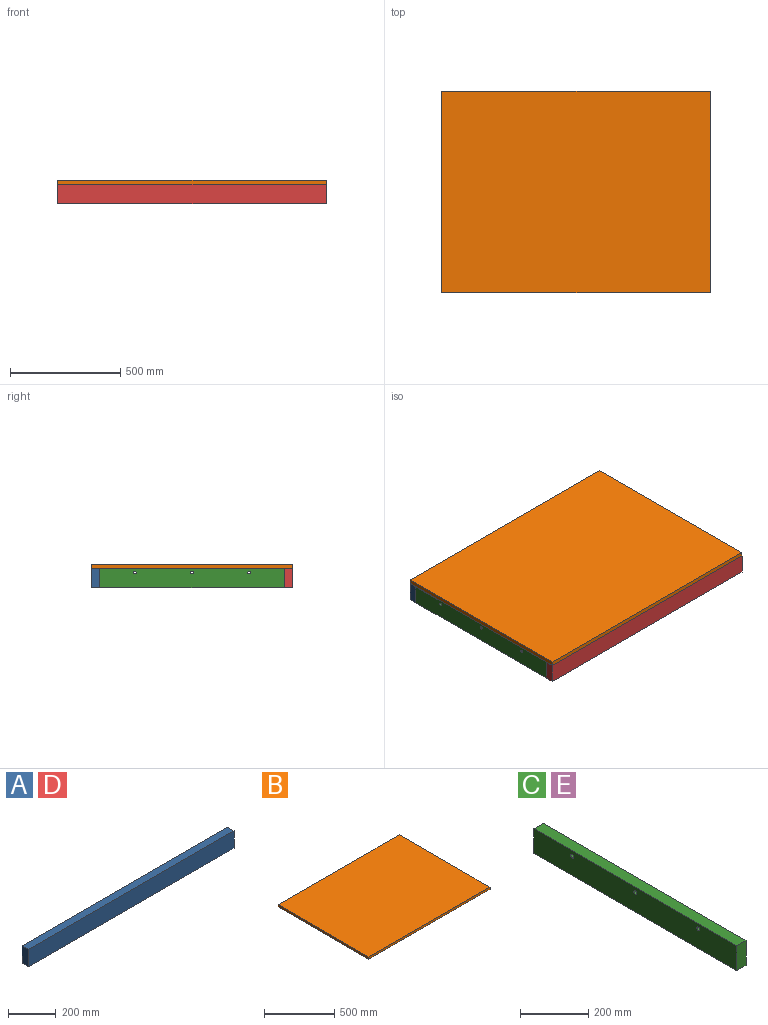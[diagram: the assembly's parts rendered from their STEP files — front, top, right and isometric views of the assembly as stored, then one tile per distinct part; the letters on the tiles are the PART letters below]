
ASSEMBLY  parts=5 mates=12
PART A: 6 faces, bbox 1219.2x38.1x88.9 mm
  f0: plane 1219.2x38.1mm, normal (0,0,1), area 46451.5mm2, adj f1,f3,f4,f5
  f1: plane 1219.2x88.9mm, normal (0,-1,0), area 108386.9mm2, adj f0,f2,f4,f5
  f2: plane 1219.2x38.1mm, normal (0,0,-1), area 46451.5mm2, adj f1,f3,f4,f5
  f3: plane 1219.2x88.9mm, normal (0,1,0), area 108386.9mm2, adj f0,f2,f4,f5
  f4: plane 88.9x38.1mm, normal (-1,0,0), area 3387.1mm2, adj f0,f1,f2,f3
  f5: plane 88.9x38.1mm, normal (1,0,0), area 3387.1mm2, adj f0,f1,f2,f3
PART B: 6 faces, bbox 1219.2x914.4x19.1 mm
  f0: plane 1219.2x19.05mm, normal (0,1,0), area 23225.8mm2, adj f1,f3,f4,f5
  f1: plane 914.4x19.05mm, normal (-1,0,0), area 17419.3mm2, adj f0,f2,f4,f5
  f2: plane 1219.2x19.05mm, normal (0,-1,0), area 23225.8mm2, adj f1,f3,f4,f5
  f3: plane 914.4x19.05mm, normal (1,0,0), area 17419.3mm2, adj f0,f2,f4,f5
  f4: plane 1219.2x914.4mm, normal (0,0,1), area 1114836.5mm2, adj f0,f1,f2,f3
  f5: plane 1219.2x914.4mm, normal (0,0,-1), area 1114836.5mm2, adj f0,f1,f2,f3
PART C: 9 faces, bbox 38.1x838.2x88.9 mm
  f0: plane 838.2x38.1mm, normal (0,0,1), area 31935.4mm2, adj f1,f3,f4,f5
  f1: plane 838.2x88.9mm, normal (-1,0,0), area 74135.9mm2, adj f0,f2,f4,f5,f6,f7,f8
  f2: plane 838.2x38.1mm, normal (0,0,-1), area 31935.4mm2, adj f1,f3,f4,f5
  f3: plane 838.2x88.9mm, normal (1,0,0), area 74135.9mm2, adj f0,f2,f4,f5,f6,f7,f8
  f4: plane 88.9x38.1mm, normal (0,1,0), area 3387.1mm2, adj f0,f1,f2,f3
  f5: plane 88.9x38.1mm, normal (0,-1,0), area 3387.1mm2, adj f0,f1,f2,f3
  f6: cylinder r=6.35mm len=38.1mm, axis (1,0,0), area 1520.1mm2, adj f1,f3
  f7: cylinder r=6.35mm len=38.1mm, axis (1,0,0), area 1520.1mm2, adj f1,f3
  f8: cylinder r=6.35mm len=38.1mm, axis (1,0,0), area 1520.1mm2, adj f1,f3
PART D: same geometry as A
PART E: same geometry as C
PLACE A t=(2481.17,1688.4,-916.47)mm
PLACE B t=(2052.69,1264.25,-824.36)mm
PLACE C t=(1383.02,754.39,-815.47)mm
PLACE D t=(2481.17,812.1,-916.47)mm
PLACE E t=(2564.12,754.39,-815.47)mm
MATE planar B.f5 <-> E.f0  axis (0,0,-1) through (1871.57,1173.49,-824.36)mm
MATE planar B.f5 <-> A.f0  axis (0,0,-1) through (1871.57,1173.49,-824.36)mm
MATE planar B.f2 <-> D.f1  axis (0,-1,0) through (1871.57,716.29,-814.84)mm
MATE planar B.f5 <-> C.f0  axis (0,0,-1) through (1871.57,1173.49,-824.36)mm
MATE planar B.f3 <-> A.f5  axis (1,0,0) through (2481.17,1173.49,-814.84)mm
MATE planar B.f3 <-> E.f3  axis (1,0,0) through (2481.17,1173.49,-814.84)mm
MATE planar D.f3 <-> C.f5  axis (0,1,0) through (1261.97,754.39,-868.81)mm
MATE planar B.f0 <-> A.f3  axis (0,1,0) through (1871.57,1630.69,-814.84)mm
MATE planar D.f4 <-> C.f1  axis (-1,0,0) through (1261.97,735.34,-868.81)mm
MATE planar D.f3 <-> E.f5  axis (0,1,0) through (2481.17,754.39,-868.81)mm
MATE planar B.f5 <-> D.f0  axis (0,0,-1) through (1871.57,1173.49,-824.36)mm
MATE planar B.f3 <-> D.f5  axis (1,0,0) through (2481.17,1173.49,-814.84)mm
